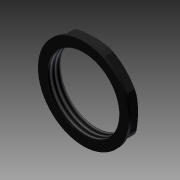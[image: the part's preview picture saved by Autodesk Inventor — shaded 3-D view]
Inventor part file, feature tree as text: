
AUTODESK INVENTOR PART (.ipt)
format: ipt  version: 2011 (Build 150239000, 239)  size: 105,472 bytes
history: native  units: mm
features: imported_body x1, thread x1
ambient origin geometry x8: Origin, YZ Plane, XZ Plane, XY Plane, X Axis, Y Axis, Z Axis, Center Point
bodies: Solid1 (feature_tree)
feature tree (2):
  imported_body  "Base1"
  thread  "Thread1"  [1 undecoded]
note: 1 required parameter value undecoded (feature->parameter linkage not recoverable at this tier; creation-order binding heuristic only, values carry confidence <= 0.55)
